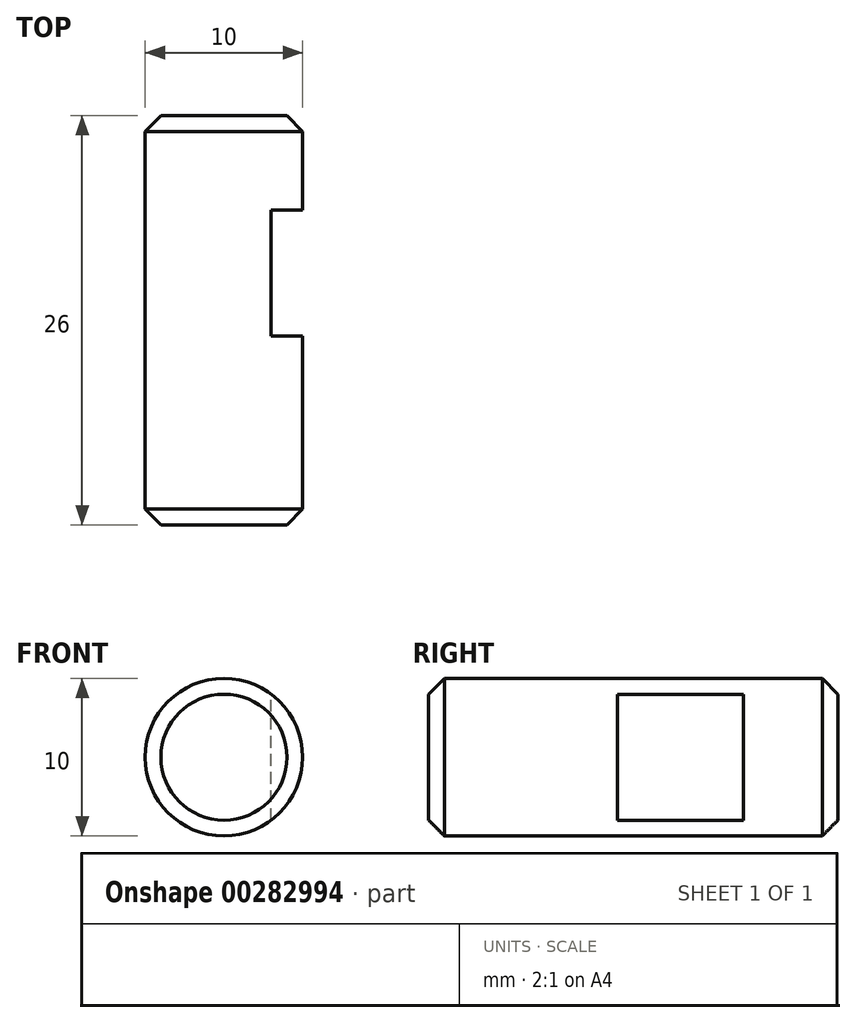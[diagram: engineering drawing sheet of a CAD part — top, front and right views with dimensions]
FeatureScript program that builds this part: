
annotation { "Feature Type Name" : "Feature", "Feature Type Description" : "" }
export const myFeature = defineFeature(function(context is Context, id is Id, definition is map)
    precondition{}
    {
        {
            var Q0;
            Q0=qCreatedBy(makeId("Front.planeOp"),FACE);
            var sketch = newSketch(context, id + "F0", { "sketchPlane" : qUnion([Q0])});
            skCircle(sketch, "E0", {"center": v(0, 0) * mm, "radius": 5 * mm});
            skSolve(sketch);
        }
        {
            var Q0;
            Q0 = qSketchRegion(id + "F0", true);
            extrude(context, id + "F1", {"entities" : qUnion([Q0]), "endBound" : BoundingType.SYMMETRIC, "depth" : 26 * mm});
        }
        {
            var Q0;
            Q0=makeQuery(id+"F1.opExtrude","CAP_EDGE",EDGE,{"disambiguationData":[OSD([sQuery(id+"F0.wireOp",EDGE,"E0")])],"isStart":false});
            var Q1;
            Q1=makeQuery(id+"F1.opExtrude","CAP_EDGE",EDGE,{"disambiguationData":[OSD([sQuery(id+"F0.wireOp",EDGE,"E0")])],"isStart":true});
            chamfer(context, id + "F2", {"entities" : qUnion([Q0, Q1]), "width" : 1 * mm, "tangentPropagation" : true});
        }
        {
            var Q0;
            Q0=qCreatedBy(makeId("Top.planeOp"),FACE);
            var sketch = newSketch(context, id + "F3", { "sketchPlane" : qUnion([Q0])});
            skLineSegment(sketch, "E1", {"start": v(-5, -12) * mm, "end": v(-5, 12) * mm, "construction": true});
            skLineSegment(sketch, "E2", {"start": v(5, 12) * mm, "end": v(5, -12) * mm, "construction": true});
            skLineSegment(sketch, "E3", {"start": v(5, 12) * mm, "end": v(4, 13) * mm, "construction": true});
            skLineSegment(sketch, "E4", {"start": v(-4, 13) * mm, "end": v(-5, 12) * mm, "construction": true});
            skLineSegment(sketch, "E5", {"start": v(-4, 13) * mm, "end": v(4, 13) * mm, "construction": true});
            skLineSegment(sketch, "E6.bottom", {"start": v(5, 7) * mm, "end": v(3, 7) * mm});
            skLineSegment(sketch, "E6.top", {"start": v(5, -1) * mm, "end": v(3, -1) * mm});
            skLineSegment(sketch, "E6.left", {"start": v(5, 7) * mm, "end": v(5, -1) * mm});
            skLineSegment(sketch, "E6.right", {"start": v(3, 7) * mm, "end": v(3, -1) * mm});
            skSolve(sketch);
        }
        {
            var Q0;
            Q0 = qSketchRegion(id + "F3", true);
            extrude(context, id + "F4", {"entities" : qUnion([Q0]), "operationType" : NewBodyOperationType.REMOVE, "endBound" : BoundingType.SYMMETRIC, "oppositeDirection" : true, "depth" : 25 * mm});
        }
    });
